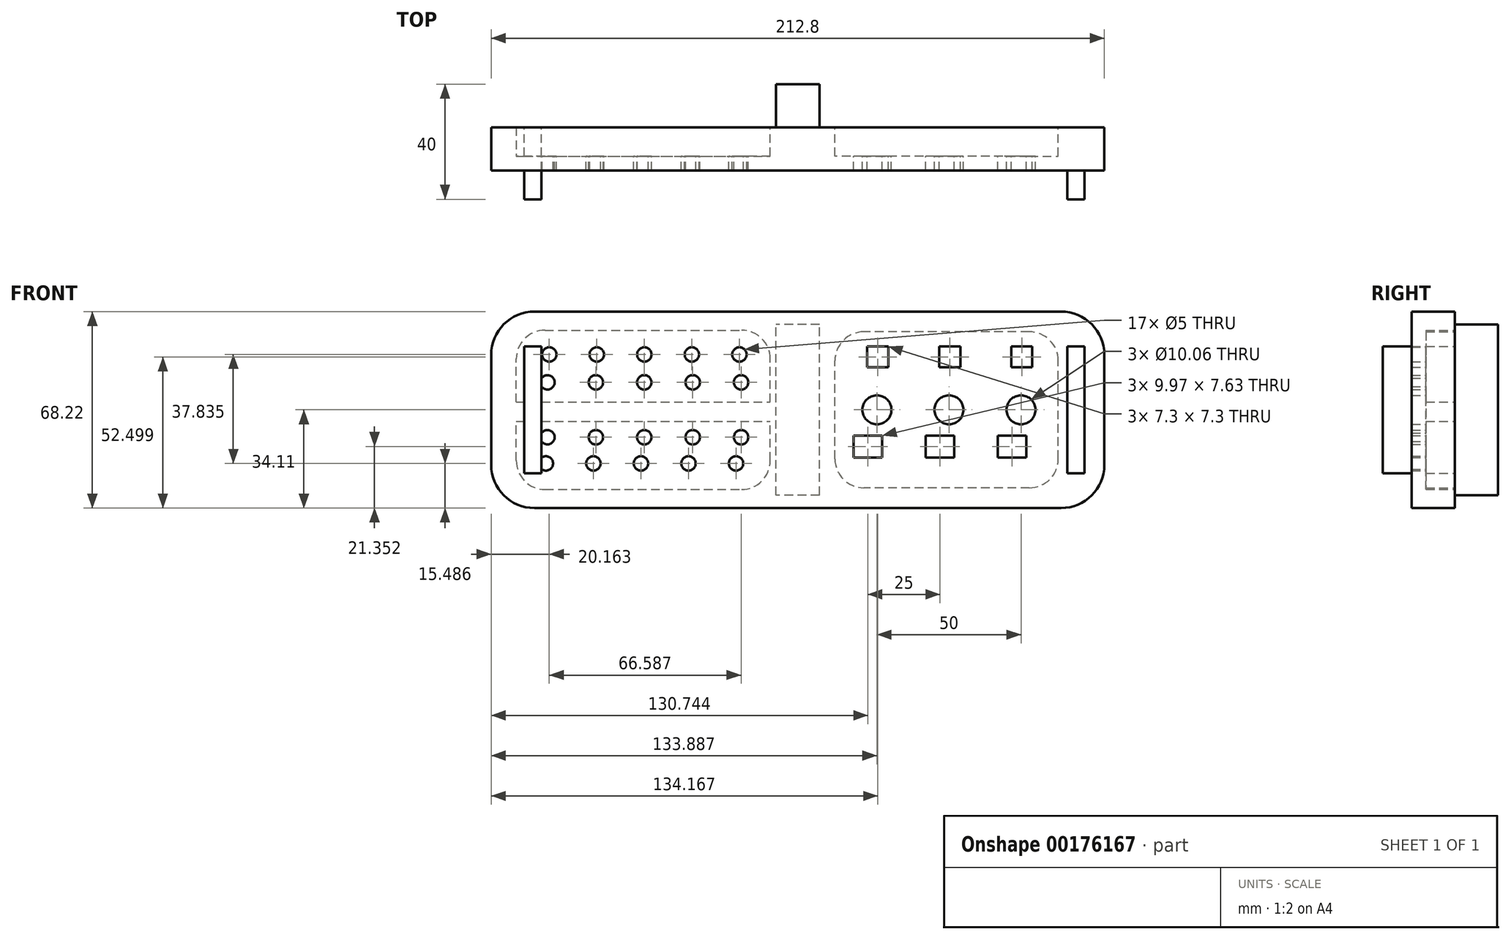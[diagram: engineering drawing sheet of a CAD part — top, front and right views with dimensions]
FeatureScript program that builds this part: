
annotation { "Feature Type Name" : "Feature", "Feature Type Description" : "" }
export const myFeature = defineFeature(function(context is Context, id is Id, definition is map)
    precondition{}
    {
        {
            var Q0;
            Q0=qCreatedBy(makeId("Front.planeOp"),FACE);
            var sketch = newSketch(context, id + "F0", { "sketchPlane" : qUnion([Q0])});
            skLineSegment(sketch, "E0.bottom", {"start": v(-91.4, -34.11) * mm, "end": v(91.4, -34.11) * mm});
            skLineSegment(sketch, "E0.top", {"start": v(-91.4, 34.11) * mm, "end": v(91.4, 34.11) * mm});
            skLineSegment(sketch, "E0.left", {"start": v(-106.4, -19.11) * mm, "end": v(-106.4, 19.11) * mm});
            skLineSegment(sketch, "E0.right", {"start": v(106.4, -19.11) * mm, "end": v(106.4, 19.11) * mm});
            skPoint(sketch, "E0.middle", {"position": v(0, 0) * mm});
            skPoint(sketch, "E1.visualSharp", {"position": v(-106.4, 34.11) * mm});
            skArc(sketch, "E1.filletArc", {"start": v(-91.4, 34.11) * mm, "mid": v(-102.01, 29.72) * mm, "end": v(-106.4, 19.11) * mm});
            skPoint(sketch, "E2.visualSharp", {"position": v(106.4, 34.11) * mm});
            skArc(sketch, "E2.filletArc", {"start": v(106.4, 19.11) * mm, "mid": v(102.01, 29.72) * mm, "end": v(91.4, 34.11) * mm});
            skPoint(sketch, "E3.visualSharp", {"position": v(106.4, -34.11) * mm});
            skArc(sketch, "E3.filletArc", {"start": v(91.4, -34.11) * mm, "mid": v(102.01, -29.72) * mm, "end": v(106.4, -19.11) * mm});
            skPoint(sketch, "E4.visualSharp", {"position": v(-106.4, -34.11) * mm});
            skArc(sketch, "E4.filletArc", {"start": v(-106.4, -19.11) * mm, "mid": v(-102.01, -29.72) * mm, "end": v(-91.4, -34.11) * mm});
            skSolve(sketch);
        }
        {
            var Q0;
            Q0 = qSketchRegion(id + "F0", true);
            extrude(context, id + "F1", {"entities" : qUnion([Q0]), "depth" : 15 * mm});
        }
        {
            var Q0;
            Q0=qCreatedBy(makeId("Front.planeOp"),FACE);
            var sketch = newSketch(context, id + "F2", { "sketchPlane" : qUnion([Q0])});
            skLineSegment(sketch, "E5.bottom", {"start": v(-87.7, -27.65) * mm, "end": v(-19.55, -27.65) * mm});
            skLineSegment(sketch, "E5.top", {"start": v(-87.7, 27.65) * mm, "end": v(-19.55, 27.65) * mm});
            skLineSegment(sketch, "E5.left", {"start": v(-97.7, -17.65) * mm, "end": v(-97.7, 17.65) * mm});
            skLineSegment(sketch, "E5.right", {"start": v(-9.55, -17.65) * mm, "end": v(-9.55, 17.65) * mm});
            skPoint(sketch, "E5.middle", {"position": v(-53.62, 0) * mm});
            skPoint(sketch, "E6.visualSharp", {"position": v(-97.7, 27.65) * mm});
            skArc(sketch, "E6.filletArc", {"start": v(-87.7, 27.65) * mm, "mid": v(-94.77, 24.72) * mm, "end": v(-97.7, 17.65) * mm});
            skPoint(sketch, "E7.visualSharp", {"position": v(-97.7, -27.65) * mm});
            skArc(sketch, "E7.filletArc", {"start": v(-97.7, -17.65) * mm, "mid": v(-94.77, -24.72) * mm, "end": v(-87.7, -27.65) * mm});
            skPoint(sketch, "E8.visualSharp", {"position": v(-9.55, -27.65) * mm});
            skArc(sketch, "E8.filletArc", {"start": v(-19.55, -27.65) * mm, "mid": v(-12.47, -24.72) * mm, "end": v(-9.55, -17.65) * mm});
            skPoint(sketch, "E9.visualSharp", {"position": v(-9.55, 27.65) * mm});
            skArc(sketch, "E9.filletArc", {"start": v(-9.55, 17.65) * mm, "mid": v(-12.47, 24.72) * mm, "end": v(-19.55, 27.65) * mm});
            skSolve(sketch);
        }
        {
            var Q0;
            Q0 = qSketchRegion(id + "F2", true);
            extrude(context, id + "F3", {"entities" : qUnion([Q0]), "operationType" : NewBodyOperationType.REMOVE, "depth" : 10 * mm});
        }
        {
            var Q0;
            Q0=makeQuery(id+"F1.opExtrude","CAP_FACE",FACE,{"disambiguationData":[OSD([sQuery(id+"F0.wireOp",EDGE,"E0.bottom"),sQuery(id+"F0.wireOp",EDGE,"E0.top"),sQuery(id+"F0.wireOp",EDGE,"E0.left"),sQuery(id+"F0.wireOp",EDGE,"E0.right"),sQuery(id+"F0.wireOp",EDGE,"E1.filletArc"),sQuery(id+"F0.wireOp",EDGE,"E2.filletArc"),sQuery(id+"F0.wireOp",EDGE,"E3.filletArc"),sQuery(id+"F0.wireOp",EDGE,"E4.filletArc")])],"isStart":true});
            var sketch = newSketch(context, id + "F4", { "sketchPlane" : qUnion([Q0])});
            skLineSegment(sketch, "E10.bottom", {"start": v(-80.4, -27.1) * mm, "end": v(-22.91, -27.1) * mm});
            skLineSegment(sketch, "E10.top", {"start": v(-80.4, 27.1) * mm, "end": v(-22.91, 27.1) * mm});
            skLineSegment(sketch, "E10.left", {"start": v(-90.4, -17.1) * mm, "end": v(-90.4, 17.1) * mm});
            skLineSegment(sketch, "E10.right", {"start": v(-12.91, -17.1) * mm, "end": v(-12.91, 17.1) * mm});
            skPoint(sketch, "E10.middle", {"position": v(-51.66, 0) * mm});
            skPoint(sketch, "E11.visualSharp", {"position": v(-90.4, 27.1) * mm});
            skArc(sketch, "E11.filletArc", {"start": v(-80.4, 27.1) * mm, "mid": v(-87.47, 24.16) * mm, "end": v(-90.4, 17.1) * mm});
            skPoint(sketch, "E12.visualSharp", {"position": v(-90.4, -27.1) * mm});
            skArc(sketch, "E12.filletArc", {"start": v(-90.4, -17.1) * mm, "mid": v(-87.47, -24.16) * mm, "end": v(-80.4, -27.1) * mm});
            skPoint(sketch, "E13.visualSharp", {"position": v(-12.91, 27.1) * mm});
            skArc(sketch, "E13.filletArc", {"start": v(-12.91, 17.1) * mm, "mid": v(-15.84, 24.16) * mm, "end": v(-22.91, 27.1) * mm});
            skPoint(sketch, "E14.visualSharp", {"position": v(-12.91, -27.1) * mm});
            skArc(sketch, "E14.filletArc", {"start": v(-22.91, -27.1) * mm, "mid": v(-15.84, -24.16) * mm, "end": v(-12.91, -17.1) * mm});
            skSolve(sketch);
        }
        {
            var Q0;
            Q0 = qSketchRegion(id + "F4", true);
            extrude(context, id + "F5", {"entities" : qUnion([Q0]), "operationType" : NewBodyOperationType.REMOVE, "oppositeDirection" : true, "depth" : 10 * mm});
        }
        {
            var Q0;
            Q0=qCreatedBy(makeId("Front.planeOp"),FACE);
            var sketch = newSketch(context, id + "F6", { "sketchPlane" : qUnion([Q0])});
            skLineSegment(sketch, "E15.bottom", {"start": v(-9.55, 2.67) * mm, "end": v(-97.98, 2.67) * mm});
            skLineSegment(sketch, "E15.top", {"start": v(-9.55, -4.07) * mm, "end": v(-97.98, -4.07) * mm});
            skLineSegment(sketch, "E15.left", {"start": v(-9.55, 2.67) * mm, "end": v(-9.55, -4.07) * mm});
            skLineSegment(sketch, "E15.right", {"start": v(-97.98, 2.67) * mm, "end": v(-97.98, -4.07) * mm});
            skSolve(sketch);
        }
        {
            var Q0;
            Q0 = qSketchRegion(id + "F6", true);
            extrude(context, id + "F7", {"entities" : qUnion([Q0]), "operationType" : NewBodyOperationType.ADD, "depth" : 15 * mm});
        }
        {
            var Q0;
            Q0=qCreatedBy(makeId("Front.planeOp"),FACE);
            var sketch = newSketch(context, id + "F8", { "sketchPlane" : qUnion([Q0])});
            skLineSegment(sketch, "E16.bottom", {"start": v(7.58, -29.62) * mm, "end": v(-7.58, -29.62) * mm});
            skLineSegment(sketch, "E16.top", {"start": v(7.58, 29.62) * mm, "end": v(-7.58, 29.62) * mm});
            skLineSegment(sketch, "E16.left", {"start": v(7.58, -29.62) * mm, "end": v(7.58, 29.62) * mm});
            skLineSegment(sketch, "E16.right", {"start": v(-7.58, -29.62) * mm, "end": v(-7.58, 29.62) * mm});
            skPoint(sketch, "E16.middle", {"position": v(0, 0) * mm});
            skSolve(sketch);
        }
        {
            var Q0;
            Q0 = qSketchRegion(id + "F8", true);
            extrude(context, id + "F9", {"entities" : qUnion([Q0]), "operationType" : NewBodyOperationType.ADD, "oppositeDirection" : true, "depth" : 15 * mm});
        }
        {
            var Q0;
            Q0=qCreatedBy(makeId("Front.planeOp"),FACE);
            var sketch = newSketch(context, id + "F10", { "sketchPlane" : qUnion([Q0])});
            skLineSegment(sketch, "E17.bottom", {"start": v(81.42, 14.74) * mm, "end": v(74.12, 14.74) * mm});
            skLineSegment(sketch, "E17.top", {"start": v(81.42, 22.04) * mm, "end": v(74.12, 22.04) * mm});
            skLineSegment(sketch, "E17.left", {"start": v(81.42, 14.74) * mm, "end": v(81.42, 22.04) * mm});
            skLineSegment(sketch, "E17.right", {"start": v(74.12, 14.74) * mm, "end": v(74.12, 22.04) * mm});
            skPoint(sketch, "E17.middle", {"position": v(77.77, 18.39) * mm});
            skLineSegment(sketch, "E18.1.0.0", {"start": v(56.42, 14.74) * mm, "end": v(49.12, 14.74) * mm});
            skLineSegment(sketch, "E18.1.0.1", {"start": v(49.12, 14.74) * mm, "end": v(49.12, 22.04) * mm});
            skLineSegment(sketch, "E18.1.0.2", {"start": v(56.42, 22.04) * mm, "end": v(49.12, 22.04) * mm});
            skLineSegment(sketch, "E18.1.0.3", {"start": v(56.42, 14.74) * mm, "end": v(56.42, 22.04) * mm});
            skLineSegment(sketch, "E18.2.0.0", {"start": v(31.42, 14.74) * mm, "end": v(24.12, 14.74) * mm});
            skLineSegment(sketch, "E18.2.0.1", {"start": v(24.12, 14.74) * mm, "end": v(24.12, 22.04) * mm});
            skLineSegment(sketch, "E18.2.0.2", {"start": v(31.42, 22.04) * mm, "end": v(24.12, 22.04) * mm});
            skLineSegment(sketch, "E18.2.0.3", {"start": v(31.42, 14.74) * mm, "end": v(31.42, 22.04) * mm});
            skLineSegment(sketch, "E18.direction1", {"start": v(74.12, 14.74) * mm, "end": v(49.12, 14.74) * mm, "construction": true});
            skCircle(sketch, "E19", {"center": v(77.49, 0) * mm, "radius": 5.03 * mm});
            skLineSegment(sketch, "E20.bottom", {"start": v(29.33, -16.57) * mm, "end": v(19.36, -16.57) * mm});
            skLineSegment(sketch, "E20.top", {"start": v(29.33, -8.95) * mm, "end": v(19.36, -8.95) * mm});
            skLineSegment(sketch, "E20.left", {"start": v(29.33, -16.57) * mm, "end": v(29.33, -8.95) * mm});
            skLineSegment(sketch, "E20.right", {"start": v(19.36, -16.57) * mm, "end": v(19.36, -8.95) * mm});
            skPoint(sketch, "E20.middle", {"position": v(24.34, -12.76) * mm});
            skLineSegment(sketch, "E21.1.0.0", {"start": v(54.33, -8.95) * mm, "end": v(44.36, -8.95) * mm});
            skLineSegment(sketch, "E21.1.0.1", {"start": v(54.33, -16.57) * mm, "end": v(54.33, -8.95) * mm});
            skLineSegment(sketch, "E21.1.0.2", {"start": v(44.36, -16.57) * mm, "end": v(44.36, -8.95) * mm});
            skLineSegment(sketch, "E21.1.0.3", {"start": v(54.33, -16.57) * mm, "end": v(44.36, -16.57) * mm});
            skLineSegment(sketch, "E21.2.0.0", {"start": v(79.33, -8.95) * mm, "end": v(69.36, -8.95) * mm});
            skLineSegment(sketch, "E21.2.0.1", {"start": v(79.33, -16.57) * mm, "end": v(79.33, -8.95) * mm});
            skLineSegment(sketch, "E21.2.0.2", {"start": v(69.36, -16.57) * mm, "end": v(69.36, -8.95) * mm});
            skLineSegment(sketch, "E21.2.0.3", {"start": v(79.33, -16.57) * mm, "end": v(69.36, -16.57) * mm});
            skLineSegment(sketch, "E21.direction1", {"start": v(19.36, -8.95) * mm, "end": v(44.36, -8.95) * mm, "construction": true});
            skCircle(sketch, "E22.1.0.0", {"center": v(52.49, 0) * mm, "radius": 5.03 * mm});
            skCircle(sketch, "E22.2.0.0", {"center": v(27.49, 0) * mm, "radius": 5.03 * mm});
            skLineSegment(sketch, "E22.direction1", {"start": v(77.49, 0) * mm, "end": v(52.49, 0) * mm, "construction": true});
            skCircle(sketch, "E23", {"center": v(-20.24, 19.21) * mm, "radius": 2.5 * mm});
            skCircle(sketch, "E24.1.0.0", {"center": v(-36.74, 19.21) * mm, "radius": 2.5 * mm});
            skCircle(sketch, "E24.2.0.0", {"center": v(-53.24, 19.21) * mm, "radius": 2.5 * mm});
            skCircle(sketch, "E24.3.0.0", {"center": v(-69.74, 19.21) * mm, "radius": 2.5 * mm});
            skCircle(sketch, "E24.4.0.0", {"center": v(-86.24, 19.21) * mm, "radius": 2.5 * mm});
            skLineSegment(sketch, "E24.direction1", {"start": v(-20.24, 19.21) * mm, "end": v(-36.74, 19.21) * mm, "construction": true});
            skCircle(sketch, "E25", {"center": v(-19.65, 9.53) * mm, "radius": 2.5 * mm});
            skCircle(sketch, "E26.1.0.0", {"center": v(-36.45, 9.53) * mm, "radius": 2.5 * mm});
            skCircle(sketch, "E26.2.0.0", {"center": v(-53.25, 9.53) * mm, "radius": 2.5 * mm});
            skCircle(sketch, "E26.3.0.0", {"center": v(-70.05, 9.53) * mm, "radius": 2.5 * mm});
            skCircle(sketch, "E26.4.0.0", {"center": v(-86.85, 9.53) * mm, "radius": 2.5 * mm});
            skLineSegment(sketch, "E26.direction1", {"start": v(-19.65, 9.53) * mm, "end": v(-36.45, 9.53) * mm, "construction": true});
            skCircle(sketch, "E27", {"center": v(-19.65, -9.53) * mm, "radius": 2.5 * mm});
            skCircle(sketch, "E28", {"center": v(-21.41, -18.62) * mm, "radius": 2.5 * mm});
            skCircle(sketch, "E29.1.0.0", {"center": v(-36.45, -9.53) * mm, "radius": 2.5 * mm});
            skCircle(sketch, "E29.2.0.0", {"center": v(-53.25, -9.53) * mm, "radius": 2.5 * mm});
            skCircle(sketch, "E29.3.0.0", {"center": v(-70.05, -9.53) * mm, "radius": 2.5 * mm});
            skCircle(sketch, "E29.4.0.0", {"center": v(-86.85, -9.53) * mm, "radius": 2.5 * mm});
            skLineSegment(sketch, "E29.direction1", {"start": v(-19.65, -9.53) * mm, "end": v(-36.45, -9.53) * mm, "construction": true});
            skCircle(sketch, "E30.1.0.0", {"center": v(-37.91, -18.62) * mm, "radius": 2.5 * mm});
            skCircle(sketch, "E30.2.0.0", {"center": v(-54.41, -18.62) * mm, "radius": 2.5 * mm});
            skCircle(sketch, "E30.3.0.0", {"center": v(-70.91, -18.62) * mm, "radius": 2.5 * mm});
            skCircle(sketch, "E30.4.0.0", {"center": v(-87.41, -18.62) * mm, "radius": 2.5 * mm});
            skLineSegment(sketch, "E30.direction1", {"start": v(-21.41, -18.62) * mm, "end": v(-37.91, -18.62) * mm, "construction": true});
            skSolve(sketch);
        }
        {
            var Q0;
            Q0 = qSketchRegion(id + "F10", true);
            extrude(context, id + "F11", {"entities" : qUnion([Q0]), "operationType" : NewBodyOperationType.REMOVE, "endBound" : BoundingType.THROUGH_ALL, "depth" : 25 * mm});
        }
        {
            var Q0;
            Q0=qCreatedBy(makeId("Front.planeOp"),FACE);
            var sketch = newSketch(context, id + "F12", { "sketchPlane" : qUnion([Q0])});
            skLineSegment(sketch, "E31.bottom", {"start": v(-88.9, -22) * mm, "end": v(-94.9, -22) * mm});
            skLineSegment(sketch, "E31.top", {"start": v(-88.9, 22) * mm, "end": v(-94.9, 22) * mm});
            skLineSegment(sketch, "E31.left", {"start": v(-88.9, -22) * mm, "end": v(-88.9, 22) * mm});
            skLineSegment(sketch, "E31.right", {"start": v(-94.9, -22) * mm, "end": v(-94.9, 22) * mm});
            skPoint(sketch, "E31.middle", {"position": v(-91.9, 0) * mm});
            skLineSegment(sketch, "E32.bottom", {"start": v(93.5, -22) * mm, "end": v(99.5, -22) * mm});
            skLineSegment(sketch, "E32.top", {"start": v(93.5, 22) * mm, "end": v(99.5, 22) * mm});
            skLineSegment(sketch, "E32.left", {"start": v(93.5, -22) * mm, "end": v(93.5, 22) * mm});
            skLineSegment(sketch, "E32.right", {"start": v(99.5, -22) * mm, "end": v(99.5, 22) * mm});
            skPoint(sketch, "E32.middle", {"position": v(96.5, 0) * mm});
            skSolve(sketch);
        }
        {
            var Q0;
            Q0 = qSketchRegion(id + "F12", true);
            extrude(context, id + "F13", {"entities" : qUnion([Q0]), "operationType" : NewBodyOperationType.ADD, "depth" : 25 * mm});
        }
    });
